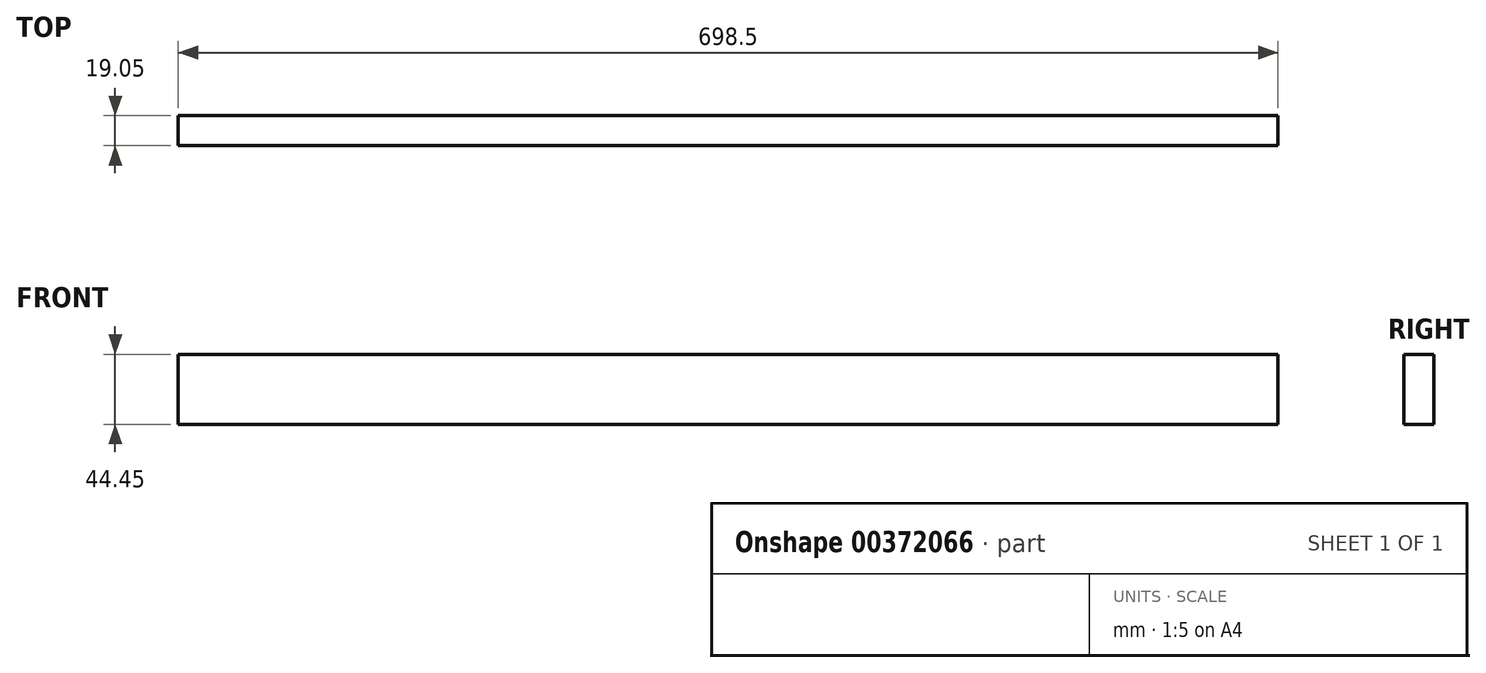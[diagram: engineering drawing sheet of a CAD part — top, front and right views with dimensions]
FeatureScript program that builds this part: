
annotation { "Feature Type Name" : "Feature", "Feature Type Description" : "" }
export const myFeature = defineFeature(function(context is Context, id is Id, definition is map)
    precondition{}
    {
        {
            var Q0;
            Q0=qCreatedBy(makeId("Front.planeOp"),FACE);
            var sketch = newSketch(context, id + "F0", { "sketchPlane" : qUnion([Q0])});
            skLineSegment(sketch, "E0.bottom", {"start": v(0, 0) * mm, "end": v(698.5, 0) * mm});
            skLineSegment(sketch, "E0.top", {"start": v(0, 44.45) * mm, "end": v(698.5, 44.45) * mm});
            skLineSegment(sketch, "E0.left", {"start": v(0, 0) * mm, "end": v(0, 44.45) * mm});
            skLineSegment(sketch, "E0.right", {"start": v(698.5, 0) * mm, "end": v(698.5, 44.45) * mm});
            skSolve(sketch);
        }
        {
            var Q0;
            Q0=makeQuery(id+"F0.imprint","IMPRINT",FACE,{"disambiguationData":[TD([[makeQuery(id+"F0.imprint","IMPRINT",EDGE,{"derivedFrom":sQuery(id+"F0.wireOp",EDGE,"E0.bottom")}),1.0]])]});
            extrude(context, id + "F1", {"entities" : qUnion([Q0]), "depth" : 19.05 * mm});
        }
    });
